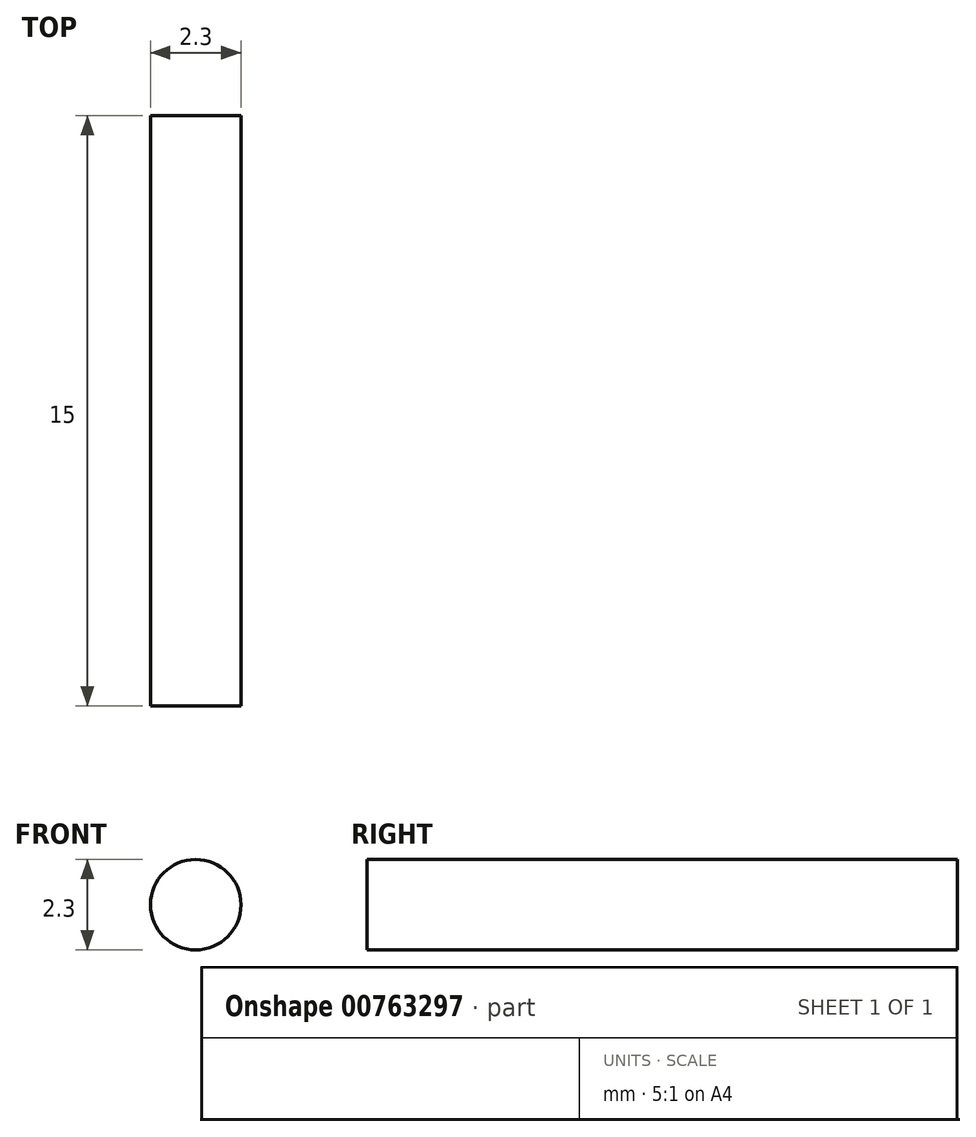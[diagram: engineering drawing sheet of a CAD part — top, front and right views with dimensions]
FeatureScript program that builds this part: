
annotation { "Feature Type Name" : "Feature", "Feature Type Description" : "" }
export const myFeature = defineFeature(function(context is Context, id is Id, definition is map)
    precondition{}
    {
        {
            var Q0;
            Q0=qCreatedBy(makeId("Front.planeOp"),FACE);
            var sketch = newSketch(context, id + "F0", { "sketchPlane" : qUnion([Q0])});
            skCircle(sketch, "E0", {"center": v(0, 0) * mm, "radius": 1.15 * mm});
            skSolve(sketch);
        }
        {
            var Q0;
            Q0=makeQuery(id+"F0.imprint","IMPRINT",FACE,{"disambiguationData":[TD([[makeQuery(id+"F0.imprint","IMPRINT",EDGE,{"derivedFrom":sQuery(id+"F0.wireOp",EDGE,"E0")}),1.0]])]});
            extrude(context, id + "F1", {"entities" : qUnion([Q0]), "oppositeDirection" : true, "depth" : 15 * mm, "offsetDistance" : 25 * mm});
        }
    });
